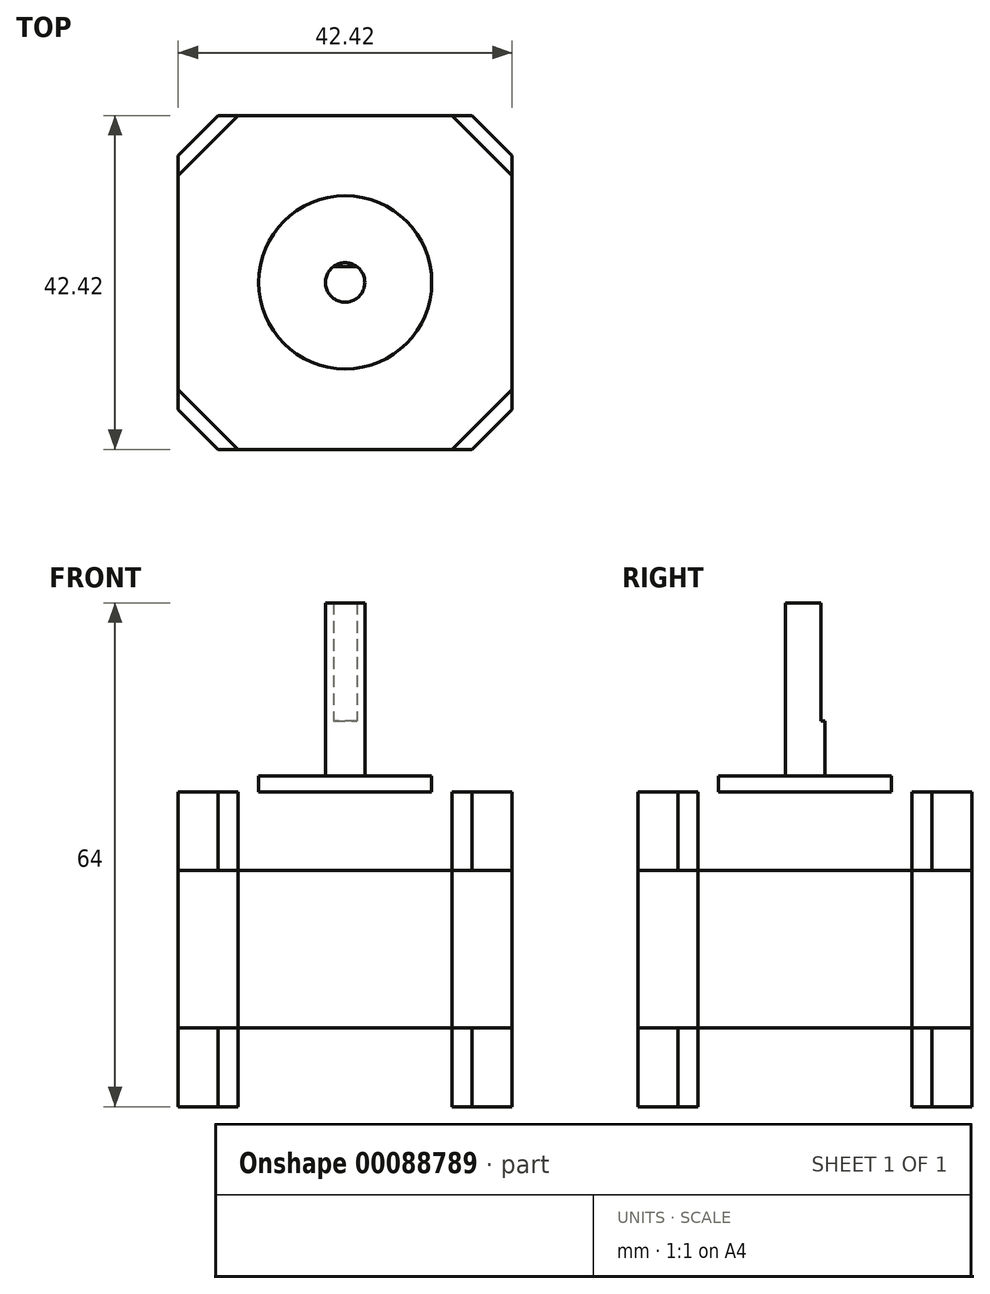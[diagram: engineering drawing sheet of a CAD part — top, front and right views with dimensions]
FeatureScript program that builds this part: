
annotation { "Feature Type Name" : "Feature", "Feature Type Description" : "" }
export const myFeature = defineFeature(function(context is Context, id is Id, definition is map)
    precondition{}
    {
        {
            var Q0;
            Q0=qCreatedBy(makeId("Top.planeOp"),FACE);
            var sketch = newSketch(context, id + "F0", { "sketchPlane" : qUnion([Q0])});
            skLineSegment(sketch, "E0.bottom", {"start": v(-21.2, 21.2) * mm, "end": v(21.2, 21.2) * mm});
            skLineSegment(sketch, "E0.top", {"start": v(-21.2, -21.2) * mm, "end": v(21.2, -21.2) * mm});
            skLineSegment(sketch, "E0.left", {"start": v(-21.2, 21.2) * mm, "end": v(-21.2, -21.2) * mm});
            skLineSegment(sketch, "E0.right", {"start": v(21.2, 21.2) * mm, "end": v(21.2, -21.2) * mm});
            skSolve(sketch);
        }
        {
            var Q0;
            Q0=makeQuery(id+"F0.imprint","IMPRINT",FACE,{"disambiguationData":[TD([[makeQuery(id+"F0.imprint","IMPRINT",EDGE,{"derivedFrom":sQuery(id+"F0.wireOp",EDGE,"E0.bottom")}),-1.0]])]});
            extrude(context, id + "F1", {"entities" : qUnion([Q0]), "depth" : 20 * mm, "symmetric" : true});
        }
        {
            var Q0;
            Q0=makeQuery(id+"F1.opExtrude","SWEPT_EDGE",EDGE,{"disambiguationData":[OSD([sQuery(id+"F0.wireOp",EDGE,"E0.bottom"),sQuery(id+"F0.wireOp",EDGE,"E0.right")])]});
            var Q1;
            Q1=makeQuery(id+"F1.opExtrude","SWEPT_EDGE",EDGE,{"disambiguationData":[OSD([sQuery(id+"F0.wireOp",EDGE,"E0.bottom"),sQuery(id+"F0.wireOp",EDGE,"E0.left")])]});
            var Q2;
            Q2=makeQuery(id+"F1.opExtrude","SWEPT_EDGE",EDGE,{"disambiguationData":[OSD([sQuery(id+"F0.wireOp",EDGE,"E0.top"),sQuery(id+"F0.wireOp",EDGE,"E0.left")])]});
            var Q3;
            Q3=makeQuery(id+"F1.opExtrude","SWEPT_EDGE",EDGE,{"disambiguationData":[OSD([sQuery(id+"F0.wireOp",EDGE,"E0.top"),sQuery(id+"F0.wireOp",EDGE,"E0.right")])]});
            chamfer(context, id + "F2", {"entities" : qUnion([Q0, Q1, Q2, Q3]), "width" : 7.62 * mm, "tangentPropagation" : true});
        }
        {
            var Q0;
            Q0=makeQuery(id+"F1.opExtrude","CAP_FACE",FACE,{"disambiguationData":[OSD([sQuery(id+"F0.wireOp",EDGE,"E0.bottom"),sQuery(id+"F0.wireOp",EDGE,"E0.top"),sQuery(id+"F0.wireOp",EDGE,"E0.left"),sQuery(id+"F0.wireOp",EDGE,"E0.right")])],"isStart":false});
            var sketch = newSketch(context, id + "F3", { "sketchPlane" : qUnion([Q0])});
            skLineSegment(sketch, "E1.bottom", {"start": v(-21.2, 21.2) * mm, "end": v(21.2, 21.2) * mm});
            skLineSegment(sketch, "E1.top", {"start": v(-21.2, -21.2) * mm, "end": v(21.2, -21.2) * mm});
            skLineSegment(sketch, "E1.left", {"start": v(-21.2, 21.2) * mm, "end": v(-21.2, -21.2) * mm});
            skLineSegment(sketch, "E1.right", {"start": v(21.2, 21.2) * mm, "end": v(21.2, -21.2) * mm});
            skSolve(sketch);
        }
        {
            var Q0;
            {var subQ0=sQuery(id+"F0.wireOp",EDGE,"E0.top");var subQ1=sQuery(id+"F0.wireOp",EDGE,"E0.right");var subQ2=sQuery(id+"F0.wireOp",EDGE,"E0.bottom");var subQ3=sQuery(id+"F0.wireOp",EDGE,"E0.left");var subQ4=makeQuery(id+"F1.opExtrude","CAP_FACE",FACE,{"disambiguationData":[OSD([subQ2,subQ0,subQ3,subQ1])],"isStart":false});var subQ8=makeQuery(id+"F2.opChamfer","BLEND_EDGE",EDGE,{"blendedFrom":[makeQuery(id+"F1.opExtrude","SWEPT_EDGE",EDGE,{"disambiguationData":[OSD([subQ2,subQ3])]}),subQ4],"blendedInto":[subQ4]});Q0=makeQuery(id+"F3.imprint","IMPRINT",FACE,{"disambiguationData":[TD([[makeQuery(id+"F3.imprint","IMPRINT",EDGE,{"derivedFrom":subQ8}),1.0]])]});}
            var Q1;
            {var subQ0=sQuery(id+"F0.wireOp",EDGE,"E0.bottom");var subQ1=sQuery(id+"F0.wireOp",EDGE,"E0.right");var subQ2=makeQuery(id+"F2.opChamfer","BLEND_EDGE",EDGE,{"blendedFrom":[makeQuery(id+"F1.opExtrude","SWEPT_EDGE",EDGE,{"disambiguationData":[OSD([subQ0,subQ1])]}),makeQuery(id+"F1.opExtrude","CAP_FACE",FACE,{"disambiguationData":[OSD([subQ0,sQuery(id+"F0.wireOp",EDGE,"E0.top"),sQuery(id+"F0.wireOp",EDGE,"E0.left"),subQ1])],"isStart":false})],"blendedInto":[makeQuery(id+"F1.opExtrude","CAP_FACE",FACE,{"disambiguationData":[OSD([subQ0,sQuery(id+"F0.wireOp",EDGE,"E0.top"),sQuery(id+"F0.wireOp",EDGE,"E0.left"),subQ1])],"isStart":false})]});Q1=makeQuery(id+"F3.imprint","IMPRINT",FACE,{"disambiguationData":[TD([[makeQuery(id+"F3.imprint","IMPRINT",EDGE,{"derivedFrom":subQ2}),-1.0]])]});}
            var Q2;
            {var subQ0=sQuery(id+"F0.wireOp",EDGE,"E0.bottom");var subQ1=sQuery(id+"F0.wireOp",EDGE,"E0.left");var subQ2=makeQuery(id+"F2.opChamfer","BLEND_EDGE",EDGE,{"blendedFrom":[makeQuery(id+"F1.opExtrude","SWEPT_EDGE",EDGE,{"disambiguationData":[OSD([subQ0,subQ1])]}),makeQuery(id+"F1.opExtrude","CAP_FACE",FACE,{"disambiguationData":[OSD([subQ0,sQuery(id+"F0.wireOp",EDGE,"E0.top"),subQ1,sQuery(id+"F0.wireOp",EDGE,"E0.right")])],"isStart":false})],"blendedInto":[makeQuery(id+"F1.opExtrude","CAP_FACE",FACE,{"disambiguationData":[OSD([subQ0,sQuery(id+"F0.wireOp",EDGE,"E0.top"),subQ1,sQuery(id+"F0.wireOp",EDGE,"E0.right")])],"isStart":false})]});Q2=makeQuery(id+"F3.imprint","IMPRINT",FACE,{"disambiguationData":[TD([[makeQuery(id+"F3.imprint","IMPRINT",EDGE,{"derivedFrom":subQ2}),-1.0]])]});}
            var Q3;
            {var subQ0=sQuery(id+"F0.wireOp",EDGE,"E0.top");var subQ1=sQuery(id+"F0.wireOp",EDGE,"E0.left");var subQ2=makeQuery(id+"F2.opChamfer","BLEND_EDGE",EDGE,{"blendedFrom":[makeQuery(id+"F1.opExtrude","SWEPT_EDGE",EDGE,{"disambiguationData":[OSD([subQ0,subQ1])]}),makeQuery(id+"F1.opExtrude","CAP_FACE",FACE,{"disambiguationData":[OSD([sQuery(id+"F0.wireOp",EDGE,"E0.bottom"),subQ0,subQ1,sQuery(id+"F0.wireOp",EDGE,"E0.right")])],"isStart":false})],"blendedInto":[makeQuery(id+"F1.opExtrude","CAP_FACE",FACE,{"disambiguationData":[OSD([sQuery(id+"F0.wireOp",EDGE,"E0.bottom"),subQ0,subQ1,sQuery(id+"F0.wireOp",EDGE,"E0.right")])],"isStart":false})]});Q3=makeQuery(id+"F3.imprint","IMPRINT",FACE,{"disambiguationData":[TD([[makeQuery(id+"F3.imprint","IMPRINT",EDGE,{"derivedFrom":subQ2}),-1.0]])]});}
            var Q4;
            {var subQ0=sQuery(id+"F0.wireOp",EDGE,"E0.top");var subQ1=sQuery(id+"F0.wireOp",EDGE,"E0.right");var subQ2=makeQuery(id+"F2.opChamfer","BLEND_EDGE",EDGE,{"blendedFrom":[makeQuery(id+"F1.opExtrude","SWEPT_EDGE",EDGE,{"disambiguationData":[OSD([subQ0,subQ1])]}),makeQuery(id+"F1.opExtrude","CAP_FACE",FACE,{"disambiguationData":[OSD([sQuery(id+"F0.wireOp",EDGE,"E0.bottom"),subQ0,sQuery(id+"F0.wireOp",EDGE,"E0.left"),subQ1])],"isStart":false})],"blendedInto":[makeQuery(id+"F1.opExtrude","CAP_FACE",FACE,{"disambiguationData":[OSD([sQuery(id+"F0.wireOp",EDGE,"E0.bottom"),subQ0,sQuery(id+"F0.wireOp",EDGE,"E0.left"),subQ1])],"isStart":false})]});Q4=makeQuery(id+"F3.imprint","IMPRINT",FACE,{"disambiguationData":[TD([[makeQuery(id+"F3.imprint","IMPRINT",EDGE,{"derivedFrom":subQ2}),-1.0]])]});}
            extrude(context, id + "F4", {"entities" : qUnion([Q0, Q1, Q2, Q3, Q4]), "operationType" : NewBodyOperationType.ADD, "depth" : 10 * mm});
        }
        {
            var Q0;
            Q0=makeQuery(id+"F4.opExtrude","SWEPT_EDGE",EDGE,{"disambiguationData":[OSD([sQuery(id+"F3.wireOp",EDGE,"E1.bottom"),sQuery(id+"F3.wireOp",EDGE,"E1.right")])]});
            var Q1;
            Q1=makeQuery(id+"F4.opExtrude","SWEPT_EDGE",EDGE,{"disambiguationData":[OSD([sQuery(id+"F3.wireOp",EDGE,"E1.bottom"),sQuery(id+"F3.wireOp",EDGE,"E1.left")])]});
            var Q2;
            Q2=makeQuery(id+"F4.opExtrude","SWEPT_EDGE",EDGE,{"disambiguationData":[OSD([sQuery(id+"F3.wireOp",EDGE,"E1.top"),sQuery(id+"F3.wireOp",EDGE,"E1.left")])]});
            var Q3;
            Q3=makeQuery(id+"F4.opExtrude","SWEPT_EDGE",EDGE,{"disambiguationData":[OSD([sQuery(id+"F3.wireOp",EDGE,"E1.top"),sQuery(id+"F3.wireOp",EDGE,"E1.right")])]});
            chamfer(context, id + "F5", {"entities" : qUnion([Q0, Q1, Q2, Q3]), "width" : 5.08 * mm, "tangentPropagation" : true});
        }
        {
            var Q0;
            Q0=makeQuery(id+"F1.opExtrude","CAP_FACE",FACE,{"disambiguationData":[OSD([sQuery(id+"F0.wireOp",EDGE,"E0.bottom"),sQuery(id+"F0.wireOp",EDGE,"E0.top"),sQuery(id+"F0.wireOp",EDGE,"E0.left"),sQuery(id+"F0.wireOp",EDGE,"E0.right")])],"isStart":true});
            var sketch = newSketch(context, id + "F6", { "sketchPlane" : qUnion([Q0])});
            skLineSegment(sketch, "E2.0.0", {"start": v(-16.13, 21.2) * mm, "end": v(16.13, 21.2) * mm});
            skLineSegment(sketch, "E2.0.1", {"start": v(16.13, 21.2) * mm, "end": v(21.2, 16.13) * mm});
            skLineSegment(sketch, "E2.0.2", {"start": v(21.2, -16.13) * mm, "end": v(21.2, 16.13) * mm});
            skLineSegment(sketch, "E2.0.3", {"start": v(21.2, -16.13) * mm, "end": v(16.13, -21.2) * mm});
            skLineSegment(sketch, "E2.0.4", {"start": v(-16.13, -21.2) * mm, "end": v(16.13, -21.2) * mm});
            skLineSegment(sketch, "E2.0.5", {"start": v(-16.13, -21.2) * mm, "end": v(-21.2, -16.13) * mm});
            skLineSegment(sketch, "E2.0.6", {"start": v(-21.2, -16.13) * mm, "end": v(-21.2, 16.13) * mm});
            skLineSegment(sketch, "E2.0.7", {"start": v(-21.2, 16.13) * mm, "end": v(-16.13, 21.2) * mm});
            skSolve(sketch);
        }
        {
            var Q0;
            {var subQ3=sQuery(id+"F6.wireOp",EDGE,"E2.0.7");Q0=makeQuery(id+"F6.imprint","IMPRINT",FACE,{"disambiguationData":[TD([[makeQuery(id+"F6.imprint","IMPRINT",EDGE,{"derivedFrom":subQ3}),-1.0]])]});}
            var Q1;
            {var subQ4=sQuery(id+"F6.wireOp",EDGE,"E2.0.1");Q1=makeQuery(id+"F6.imprint","IMPRINT",FACE,{"disambiguationData":[TD([[makeQuery(id+"F6.imprint","IMPRINT",EDGE,{"derivedFrom":subQ4}),-1.0]])]});}
            var Q2;
            {var subQ4=sQuery(id+"F6.wireOp",EDGE,"E2.0.3");Q2=makeQuery(id+"F6.imprint","IMPRINT",FACE,{"disambiguationData":[TD([[makeQuery(id+"F6.imprint","IMPRINT",EDGE,{"derivedFrom":subQ4}),-1.0]])]});}
            var Q3;
            {var subQ4=sQuery(id+"F6.wireOp",EDGE,"E2.0.5");Q3=makeQuery(id+"F6.imprint","IMPRINT",FACE,{"disambiguationData":[TD([[makeQuery(id+"F6.imprint","IMPRINT",EDGE,{"derivedFrom":subQ4}),-1.0]])]});}
            var Q4;
            {var subQ0=sQuery(id+"F0.wireOp",EDGE,"E0.top");var subQ1=sQuery(id+"F0.wireOp",EDGE,"E0.right");var subQ2=sQuery(id+"F0.wireOp",EDGE,"E0.bottom");var subQ3=sQuery(id+"F0.wireOp",EDGE,"E0.left");var subQ4=makeQuery(id+"F1.opExtrude","CAP_FACE",FACE,{"disambiguationData":[OSD([subQ2,subQ0,subQ3,subQ1])],"isStart":true});var subQ8=makeQuery(id+"F2.opChamfer","BLEND_EDGE",EDGE,{"blendedFrom":[makeQuery(id+"F1.opExtrude","SWEPT_EDGE",EDGE,{"disambiguationData":[OSD([subQ2,subQ3])]}),subQ4],"blendedInto":[subQ4]});Q4=makeQuery(id+"F6.imprint","IMPRINT",FACE,{"disambiguationData":[TD([[makeQuery(id+"F6.imprint","IMPRINT",EDGE,{"derivedFrom":subQ8}),1.0]])]});}
            extrude(context, id + "F7", {"entities" : qUnion([Q0, Q1, Q2, Q3, Q4]), "operationType" : NewBodyOperationType.ADD, "depth" : 10 * mm});
        }
        {
            var Q0;
            Q0=makeQuery(id+"F4.opExtrude","CAP_FACE",FACE,{"disambiguationData":[OSD([sQuery(id+"F3.wireOp",EDGE,"E1.bottom"),sQuery(id+"F3.wireOp",EDGE,"E1.top"),sQuery(id+"F3.wireOp",EDGE,"E1.left"),sQuery(id+"F3.wireOp",EDGE,"E1.right")])],"isStart":false});
            var sketch = newSketch(context, id + "F8", { "sketchPlane" : qUnion([Q0])});
            skCircle(sketch, "E3", {"center": v(0, 0) * mm, "radius": 11 * mm});
            skSolve(sketch);
        }
        {
            var Q0;
            Q0=makeQuery(id+"F8.imprint","IMPRINT",FACE,{"disambiguationData":[TD([[makeQuery(id+"F8.imprint","IMPRINT",EDGE,{"derivedFrom":sQuery(id+"F8.wireOp",EDGE,"E3")}),1.0]])]});
            extrude(context, id + "F9", {"entities" : qUnion([Q0]), "operationType" : NewBodyOperationType.ADD, "depth" : 2 * mm});
        }
        {
            var Q0;
            Q0=makeQuery(id+"F9.opExtrude","CAP_FACE",FACE,{"disambiguationData":[OSD([sQuery(id+"F8.wireOp",EDGE,"E3")])],"isStart":false});
            var sketch = newSketch(context, id + "F10", { "sketchPlane" : qUnion([Q0])});
            skCircle(sketch, "E4", {"center": v(0, 0) * mm, "radius": 2.5 * mm});
            skSolve(sketch);
        }
        {
            var Q0;
            Q0=makeQuery(id+"F10.imprint","IMPRINT",FACE,{"disambiguationData":[TD([[makeQuery(id+"F10.imprint","IMPRINT",EDGE,{"derivedFrom":sQuery(id+"F10.wireOp",EDGE,"E4")}),1.0]])]});
            extrude(context, id + "F11", {"entities" : qUnion([Q0]), "depth" : 22 * mm});
        }
        {
            var Q0;
            Q0=makeQuery(id+"F11.opExtrude","CAP_FACE",FACE,{"disambiguationData":[OSD([sQuery(id+"F10.wireOp",EDGE,"E4")])],"isStart":false});
            var sketch = newSketch(context, id + "F12", { "sketchPlane" : qUnion([Q0])});
            skLineSegment(sketch, "E5.bottom", {"start": v(-2.63, 2.93) * mm, "end": v(2.62, 2.93) * mm});
            skLineSegment(sketch, "E5.top", {"start": v(-2.63, 2) * mm, "end": v(2.62, 2) * mm});
            skLineSegment(sketch, "E5.left", {"start": v(-2.63, 2.93) * mm, "end": v(-2.63, 2) * mm});
            skLineSegment(sketch, "E5.right", {"start": v(2.62, 2.93) * mm, "end": v(2.62, 2) * mm});
            skSolve(sketch);
        }
        {
            var Q0;
            {var subQ0=makeQuery(id+"F11.opExtrude","CAP_EDGE",EDGE,{"disambiguationData":[OSD([sQuery(id+"F10.wireOp",EDGE,"E4")])],"isStart":false});var subQ1=sQuery(id+"F12.wireOp",EDGE,"E5.top");var subQ3=makeQuery(id+"F12.imprint","INTERSECT",VERTEX,{"disambiguationData":[OD(0.0)],"derivedFrom":[subQ0,subQ1]});Q0=qUnion([makeQuery(id+"F12.imprint","IMPRINT",FACE,{"disambiguationData":[TD([[makeQuery(id+"F12.imprint","IMPRINT",EDGE,{"derivedFrom":sQuery(id+"F12.wireOp",EDGE,"E5.bottom")}),-1.0]])]}),makeQuery(id+"F12.imprint","IMPRINT",FACE,{"disambiguationData":[TD([[makeQuery(id+"F12.imprint","IMPRINT",EDGE,{"disambiguationData":[TD([[subQ3,-1.0]])],"derivedFrom":subQ1}),1.0]])]})]);}
            extrude(context, id + "F13", {"entities" : qUnion([Q0]), "operationType" : NewBodyOperationType.REMOVE, "oppositeDirection" : true, "depth" : 15 * mm});
        }
        {
            var Q0;
            Q0=makeQuery(id+"F4.opExtrude","CAP_FACE",FACE,{"disambiguationData":[OSD([sQuery(id+"F3.wireOp",EDGE,"E1.bottom"),sQuery(id+"F3.wireOp",EDGE,"E1.top"),sQuery(id+"F3.wireOp",EDGE,"E1.left"),sQuery(id+"F3.wireOp",EDGE,"E1.right")])],"isStart":false});
            var sketch = newSketch(context, id + "F14", { "sketchPlane" : qUnion([Q0])});
            skCircle(sketch, "E6", {"center": v(-15.5, 15.5) * mm, "radius": 1.5 * mm});
            skCircle(sketch, "E7", {"center": v(15.5, 15.5) * mm, "radius": 1.5 * mm});
            skCircle(sketch, "E8", {"center": v(15.5, -15.5) * mm, "radius": 1.5 * mm});
            skCircle(sketch, "E9", {"center": v(-15.5, -15.5) * mm, "radius": 1.5 * mm});
            skLineSegment(sketch, "E10", {"start": v(-45.53, 0) * mm, "end": v(50.04, 0) * mm, "construction": true});
            skLineSegment(sketch, "E11", {"start": v(0, -35.63) * mm, "end": v(0, 35.98) * mm, "construction": true});
            skLineSegment(sketch, "E12.rect.bottom", {"start": v(-15.5, 15.5) * mm, "end": v(15.5, 15.5) * mm, "construction": true});
            skLineSegment(sketch, "E12.rect.top", {"start": v(-15.5, -15.5) * mm, "end": v(15.5, -15.5) * mm, "construction": true});
            skLineSegment(sketch, "E12.rect.left", {"start": v(-15.5, 15.5) * mm, "end": v(-15.5, -15.5) * mm, "construction": true});
            skLineSegment(sketch, "E12.rect.right", {"start": v(15.5, 15.5) * mm, "end": v(15.5, -15.5) * mm, "construction": true});
            skPoint(sketch, "E12.rect.middle", {"position": v(0, 0) * mm});
            skPoint(sketch, "E13", {"position": v(0, 15.5) * mm});
            skSolve(sketch);
        }
        {
            var Q0;
            {Q0=qUnion([makeQuery(id+"F14.imprint","IMPRINT",FACE,{"disambiguationData":[TD([[makeQuery(id+"F14.imprint","IMPRINT",EDGE,{"derivedFrom":sQuery(id+"F14.wireOp",EDGE,"E6")}),1.0]])]}),makeQuery(id+"F14.imprint","IMPRINT",FACE,{"disambiguationData":[TD([[makeQuery(id+"F14.imprint","IMPRINT",EDGE,{"derivedFrom":sQuery(id+"F14.wireOp",EDGE,"E7")}),1.0]])]}),makeQuery(id+"F14.imprint","IMPRINT",FACE,{"disambiguationData":[TD([[makeQuery(id+"F14.imprint","IMPRINT",EDGE,{"derivedFrom":sQuery(id+"F14.wireOp",EDGE,"E8")}),1.0]])]}),makeQuery(id+"F14.imprint","IMPRINT",FACE,{"disambiguationData":[TD([[makeQuery(id+"F14.imprint","IMPRINT",EDGE,{"derivedFrom":sQuery(id+"F14.wireOp",EDGE,"E9")}),1.0]])]})]);}
            extrude(context, id + "F15", {"entities" : qUnion([Q0]), "operationType" : NewBodyOperationType.REMOVE, "oppositeDirection" : true, "depth" : 6.35 * mm});
        }
    });
